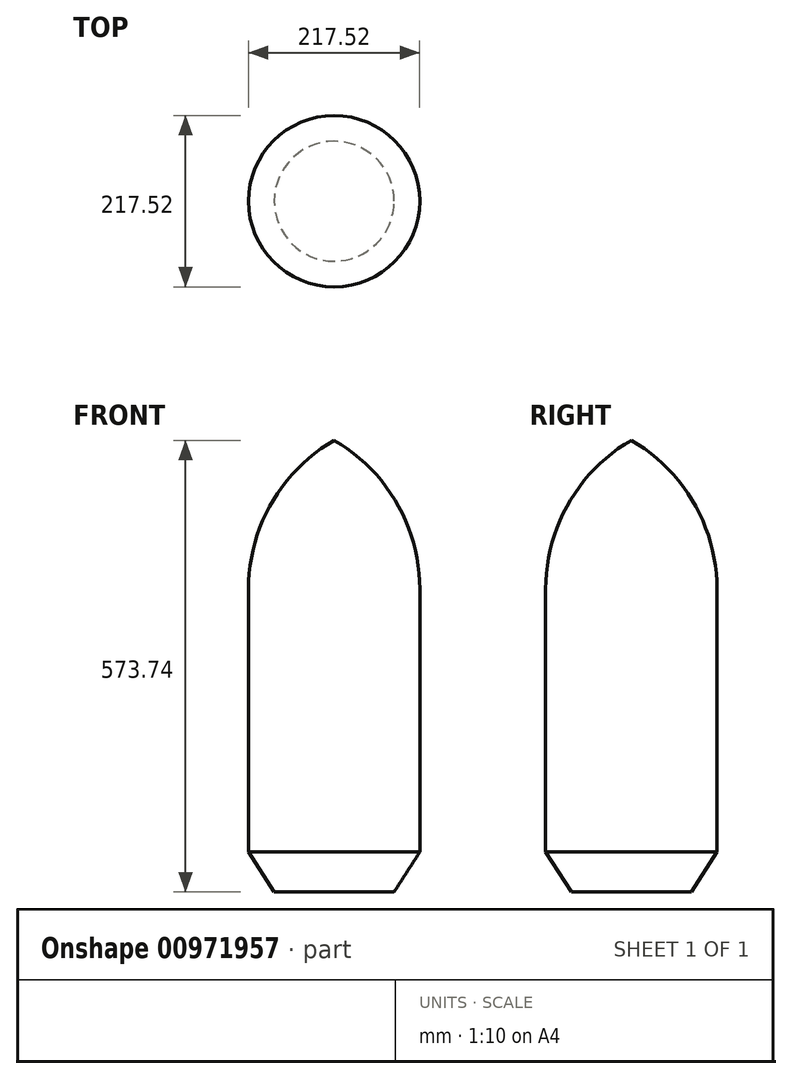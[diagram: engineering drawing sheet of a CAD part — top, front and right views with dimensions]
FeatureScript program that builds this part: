
annotation { "Feature Type Name" : "Feature", "Feature Type Description" : "" }
export const myFeature = defineFeature(function(context is Context, id is Id, definition is map)
    precondition{}
    {
        {
            var Q0;
            Q0=qCreatedBy(makeId("Front.planeOp"),FACE);
            var sketch = newSketch(context, id + "F0", { "sketchPlane" : qUnion([Q0])});
            skLineSegment(sketch, "E0", {"start": v(0, 0) * mm, "end": v(0, 79.28) * mm});
            skLineSegment(sketch, "E1", {"start": v(0, 79.28) * mm, "end": v(0, -63.58) * mm});
            skLineSegment(sketch, "E2", {"start": v(0, -63.58) * mm, "end": v(-18.98, -63.58) * mm});
            skLineSegment(sketch, "E3", {"start": v(-18.98, -63.58) * mm, "end": v(-27.08, -50.96) * mm});
            skLineSegment(sketch, "E4", {"start": v(-27.08, -50.96) * mm, "end": v(-27.08, 32.25) * mm});
            skArc(sketch, "E5", {"start": v(0, 79.28) * mm, "mid": v(-19.83, 59.38) * mm, "end": v(-27.08, 32.25) * mm});
            skSolve(sketch);
        }
        {
            var Q0;
            {var subQ0=sQuery(id+"F0.wireOp",EDGE,"E2");Q0=makeQuery(id+"F0.imprint","IMPRINT",FACE,{"disambiguationData":[TD([[makeQuery(id+"F0.imprint","IMPRINT",EDGE,{"derivedFrom":subQ0}),-1.0]])]});}
            var Q1;
            Q1=sQuery(id+"F0.wireOp",EDGE,"E1");
            revolve(context, id + "F1", {"surfaceOperationType" : NewSurfaceOperationType.NEW, "entities" : qUnion([Q0]), "axis" : qUnion([Q1]), "revolveType" : RevolveType.FULL});
        }
        {
            var Q0;
            Q0=makeQuery(id+"F1.opRevolve","SWEPT_BODY",BODY,{"disambiguationData":[OSD([sQuery(id+"F0.wireOp",EDGE,"E1"),sQuery(id+"F0.wireOp",EDGE,"E2"),sQuery(id+"F0.wireOp",EDGE,"E3"),sQuery(id+"F0.wireOp",EDGE,"E4"),sQuery(id+"F0.wireOp",EDGE,"E5")])]});
            var Q1;
            Q1=sQuery(id+"F0.wireOp",VERTEX,"E0.start");
            transform(context, id + "F2", {"entities" : qUnion([Q0]), "transformType" : TransformType.SCALE_UNIFORMLY, "scale" : 4.02, "scalePoint" : qUnion([Q1]), "makeCopy" : false});
        }
    });
